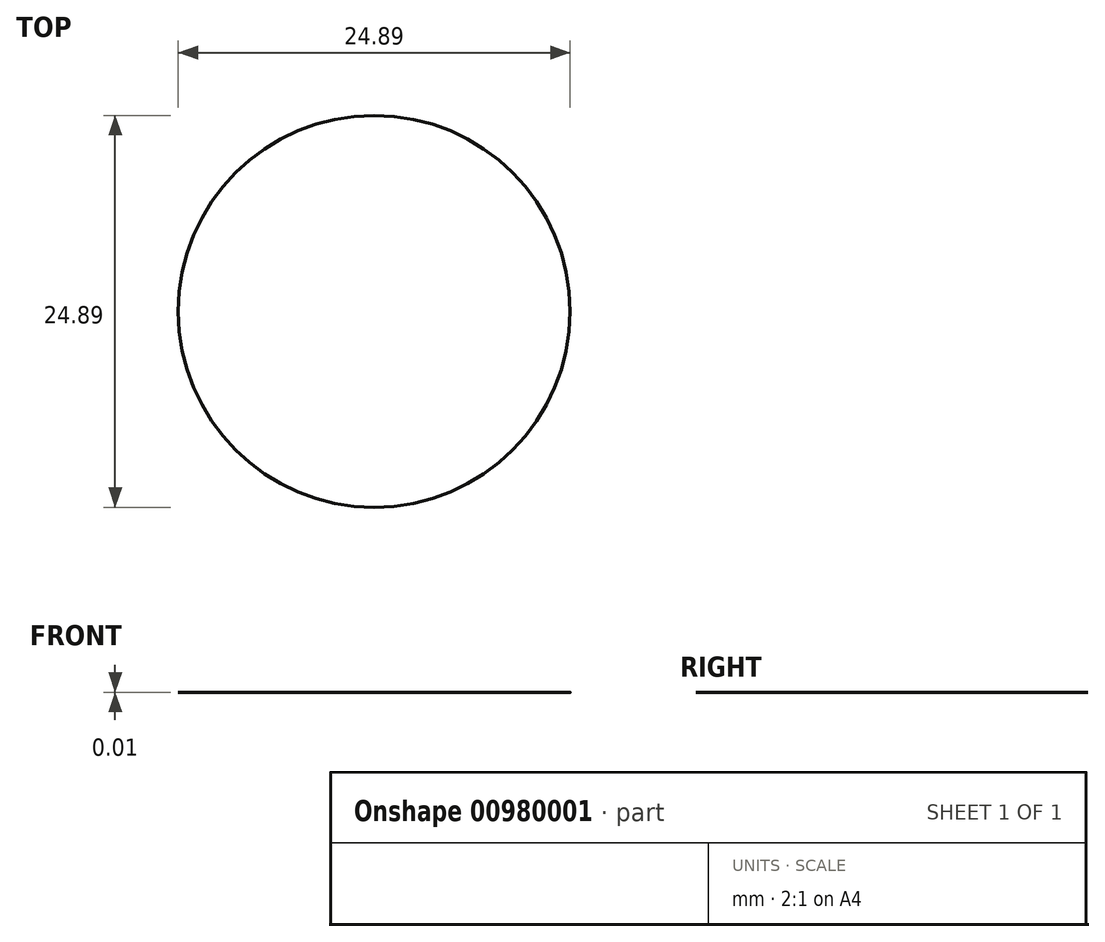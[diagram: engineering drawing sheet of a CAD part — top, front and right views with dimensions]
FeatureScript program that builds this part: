
annotation { "Feature Type Name" : "Feature", "Feature Type Description" : "" }
export const myFeature = defineFeature(function(context is Context, id is Id, definition is map)
    precondition{}
    {
        {
            var Q0;
            Q0=qCreatedBy(makeId("Top.planeOp"),FACE);
            var sketch = newSketch(context, id + "F0", { "sketchPlane" : qUnion([Q0])});
            skCircle(sketch, "E0", {"center": v(-40.74, 28.78) * mm, "radius": 12.45 * mm});
            skSolve(sketch);
        }
        {
            var Q0;
            Q0=makeQuery(id+"F0.imprint","IMPRINT",FACE,{"disambiguationData":[TD([[makeQuery(id+"F0.imprint","IMPRINT",EDGE,{"derivedFrom":sQuery(id+"F0.wireOp",EDGE,"E0")}),1.0]])]});
            var sketch = newSketch(context, id + "F1", { "sketchPlane" : qUnion([Q0])});
            skCircle(sketch, "E1", {"center": v(-40.74, 28.78) * mm, "radius": 9.92 * mm});
            skSolve(sketch);
        }
        {
            var Q0;
            Q0=makeQuery(id+"F0.imprint","IMPRINT",FACE,{"disambiguationData":[TD([[makeQuery(id+"F0.imprint","IMPRINT",EDGE,{"derivedFrom":sQuery(id+"F0.wireOp",EDGE,"E0")}),1.0]])]});
            extrude(context, id + "F2", {"entities" : qUnion([Q0]), "depth" : 6 / 812.8 * mm, "offsetDistance" : 25.4 * mm});
        }
        {
            var Q0;
            Q0=makeQuery(id+"F1.imprint","IMPRINT",FACE,{"disambiguationData":[TD([[makeQuery(id+"F1.imprint","IMPRINT",EDGE,{"derivedFrom":sQuery(id+"F1.wireOp",EDGE,"E1")}),1.0]])]});
            var Q1;
            Q1=sQuery(id+"F1.wireOp",EDGE,"E1");
            extrude(context, id + "F3", {"entities" : qUnion([Q0]), "bodyType" : ToolBodyType.SURFACE, "operationType" : NewBodyOperationType.ADD, "surfaceEntities" : qUnion([Q1]), "oppositeDirection" : true, "depth" : 4.76 * mm, "offsetDistance" : 25.4 * mm});
        }
    });
